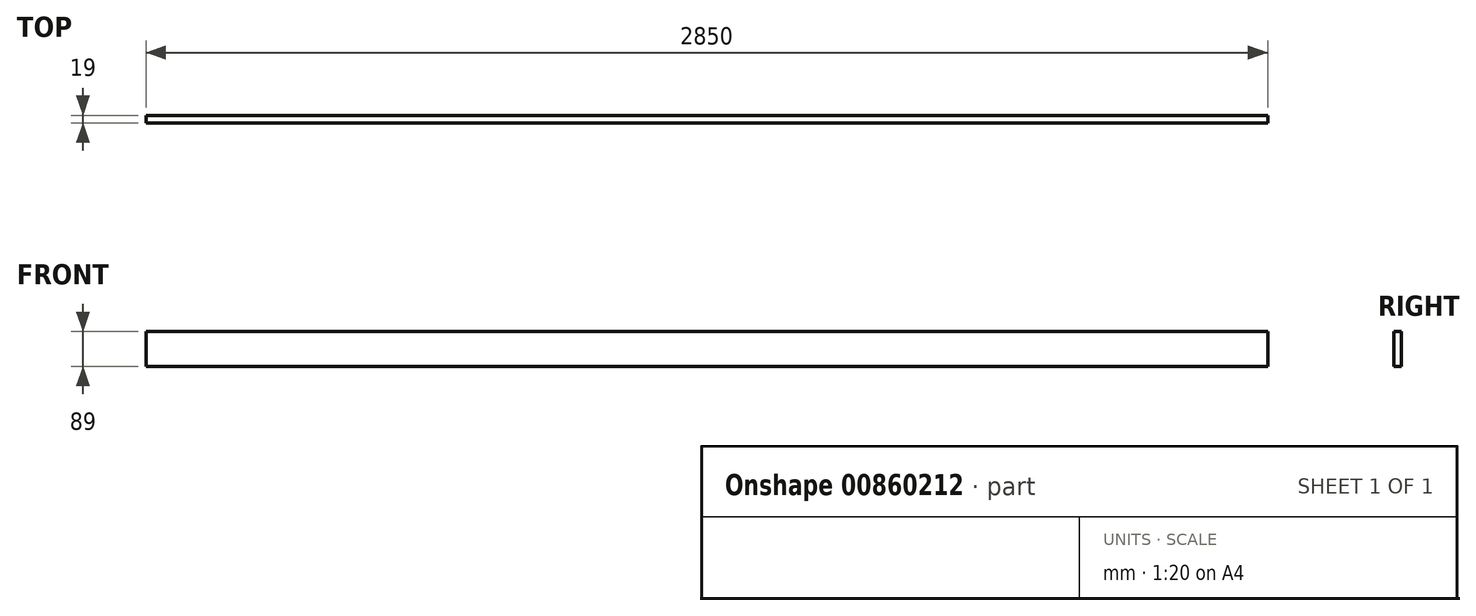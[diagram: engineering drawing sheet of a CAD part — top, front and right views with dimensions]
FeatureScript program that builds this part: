
annotation { "Feature Type Name" : "Feature", "Feature Type Description" : "" }
export const myFeature = defineFeature(function(context is Context, id is Id, definition is map)
    precondition{}
    {
        {
            var Q0;
            Q0=qCreatedBy(makeId("Right.planeOp"),FACE);
            var sketch = newSketch(context, id + "F0", { "sketchPlane" : qUnion([Q0])});
            skLineSegment(sketch, "E0.bottom", {"start": v(0, 0) * mm, "end": v(19, 0) * mm});
            skLineSegment(sketch, "E0.top", {"start": v(0, 89) * mm, "end": v(19, 89) * mm});
            skLineSegment(sketch, "E0.left", {"start": v(0, 0) * mm, "end": v(0, 89) * mm});
            skLineSegment(sketch, "E0.right", {"start": v(19, 0) * mm, "end": v(19, 89) * mm});
            skSolve(sketch);
        }
        {
            var Q0;
            Q0=makeQuery(id+"F0.imprint","IMPRINT",FACE,{"disambiguationData":[TD([[makeQuery(id+"F0.imprint","IMPRINT",EDGE,{"derivedFrom":sQuery(id+"F0.wireOp",EDGE,"E0.bottom")}),1.0]])]});
            extrude(context, id + "F1", {"entities" : qUnion([Q0]), "depth" : 2850 * mm, "offsetDistance" : 25 * mm});
        }
    });
